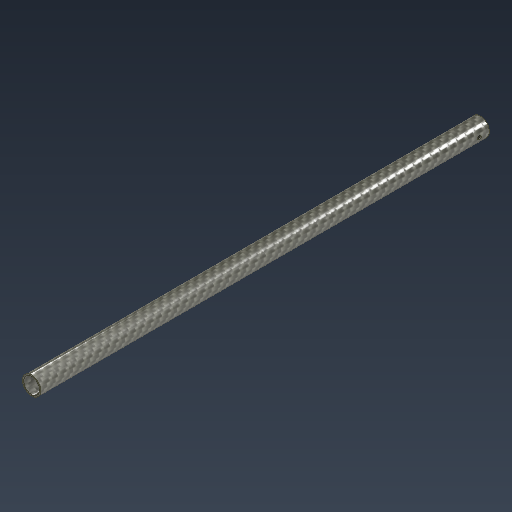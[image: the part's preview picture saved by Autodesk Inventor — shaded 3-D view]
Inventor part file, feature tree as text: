
AUTODESK INVENTOR PART (.ipt)
format: ipt  version: 2024.1 (Build 281209000, 209)  size: 139,264 bytes
history: native  units: mm
features: extrude x2, sketch x1
ambient origin geometry x8: Origin, YZ Plane, XZ Plane, XY Plane, X Axis, Y Axis, Z Axis, Center Point
bodies: Solid1 (feature_tree)
feature tree (3):
  extrude  "Extrusion1"  Depth=8.75mm
  extrude  "Extrusion2"  Depth=8.75mm TaperAngle=0.0deg
  sketch  "Sketch2"  dims[d0=16.0mm d1=14.0mm d2=390.0mm d3=0.0mm d4=8.75mm d5=3.2mm d6=0.0mm d7=0.0mm]
